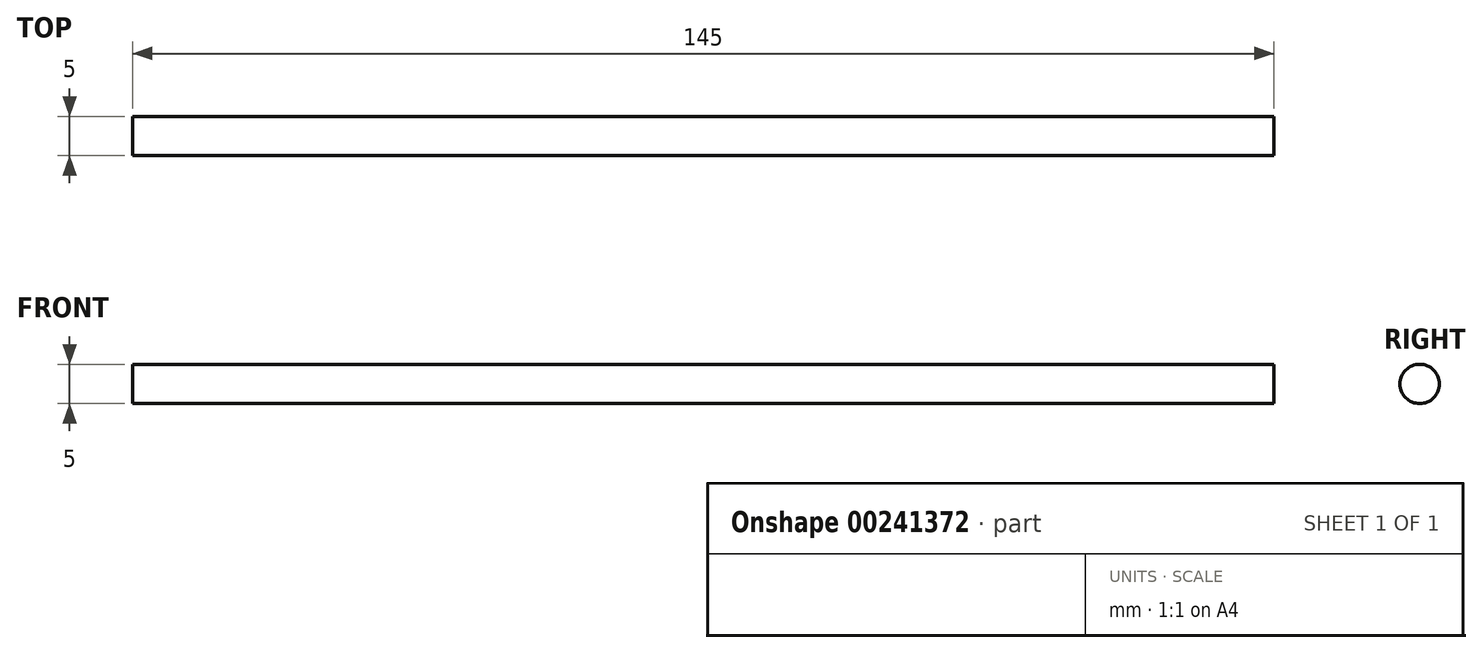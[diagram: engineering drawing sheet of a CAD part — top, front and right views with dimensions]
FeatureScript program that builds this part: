
annotation { "Feature Type Name" : "Feature", "Feature Type Description" : "" }
export const myFeature = defineFeature(function(context is Context, id is Id, definition is map)
    precondition{}
    {
        {
            var Q0;
            Q0=qCreatedBy(makeId("Right.planeOp"),FACE);
            var sketch = newSketch(context, id + "F0", { "sketchPlane" : qUnion([Q0])});
            skCircle(sketch, "E0", {"center": v(0, 0) * mm, "radius": 2.5 * mm});
            skSolve(sketch);
        }
        {
            var Q0;
            Q0 = qSketchRegion(id + "F0", true);
            extrude(context, id + "F1", {"entities" : qUnion([Q0]), "depth" : 145 * mm});
        }
    });
